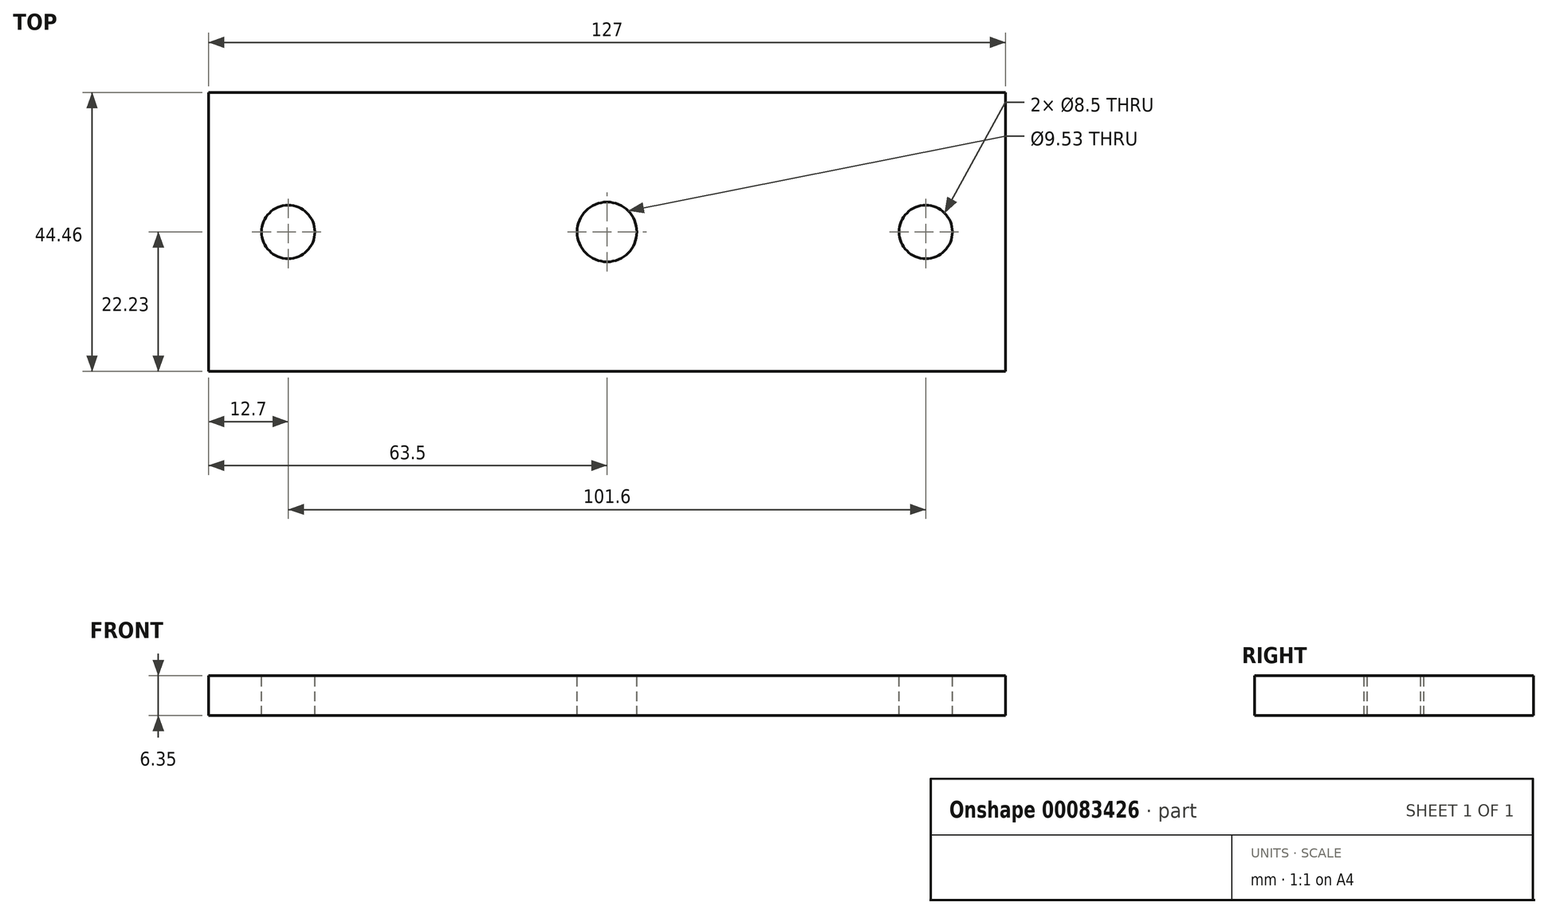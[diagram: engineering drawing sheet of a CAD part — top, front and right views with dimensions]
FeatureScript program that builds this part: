
annotation { "Feature Type Name" : "Feature", "Feature Type Description" : "" }
export const myFeature = defineFeature(function(context is Context, id is Id, definition is map)
    precondition{}
    {
        {
            var Q0;
            Q0=qCreatedBy(makeId("Top.planeOp"),FACE);
            var sketch = newSketch(context, id + "F0", { "sketchPlane" : qUnion([Q0])});
            skLineSegment(sketch, "E0.bottom", {"start": v(-63.5, 22.23) * mm, "end": v(63.5, 22.23) * mm});
            skLineSegment(sketch, "E0.top", {"start": v(-63.5, -22.23) * mm, "end": v(63.5, -22.23) * mm});
            skLineSegment(sketch, "E0.left", {"start": v(-63.5, 22.23) * mm, "end": v(-63.5, -22.23) * mm});
            skLineSegment(sketch, "E0.right", {"start": v(63.5, 22.23) * mm, "end": v(63.5, -22.23) * mm});
            skPoint(sketch, "E0.middle", {"position": v(0, 0) * mm});
            skSolve(sketch);
        }
        {
            var Q0;
            Q0 = qSketchRegion(id + "F0", true);
            extrude(context, id + "F1", {"entities" : qUnion([Q0]), "depth" : 6.35 * mm});
        }
        {
            var Q0;
            Q0=makeQuery(id+"F1.opExtrude","CAP_FACE",FACE,{"disambiguationData":[OSD([sQuery(id+"F0.wireOp",EDGE,"E0.bottom"),sQuery(id+"F0.wireOp",EDGE,"E0.top"),sQuery(id+"F0.wireOp",EDGE,"E0.left"),sQuery(id+"F0.wireOp",EDGE,"E0.right")])],"isStart":false});
            var sketch = newSketch(context, id + "F2", { "sketchPlane" : qUnion([Q0])});
            skLineSegment(sketch, "E1", {"start": v(-63.5, 0) * mm, "end": v(63.5, 0) * mm});
            skCircle(sketch, "E2", {"center": v(0, 0) * mm, "radius": 4.76 * mm});
            skCircle(sketch, "E3", {"center": v(-50.8, 0) * mm, "radius": 4.25 * mm});
            skCircle(sketch, "E4.MirrorC", {"center": v(50.8, 0) * mm, "radius": 4.25 * mm});
            skSolve(sketch);
        }
        {
            var Q0;
            Q0 = qSketchRegion(id + "F2", true);
            extrude(context, id + "F3", {"entities" : qUnion([Q0]), "operationType" : NewBodyOperationType.REMOVE, "endBound" : BoundingType.UP_TO_NEXT, "oppositeDirection" : true, "depth" : 25.4 * mm});
        }
    });
